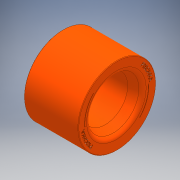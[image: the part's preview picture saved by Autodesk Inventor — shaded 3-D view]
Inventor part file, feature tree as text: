
AUTODESK INVENTOR PART (.ipt)
format: ipt  version: 2019.4 (Build 234330000, 330)  size: 897,536 bytes
history: native  units: mm
features: fillet x5, revolve x1, plane x1, emboss x1, sketch x1
ambient origin geometry x8: Origin, YZ Plane, XZ Plane, XY Plane, X Axis, Y Axis, Z Axis, Center Point
bodies: Solid1 (feature_tree)
feature tree (9):
  revolve  "Revolution1"  [1 undecoded]
  fillet  "Fillet8"  Radius=69.5mm
  fillet  "Fillet9"  Radius=63.0mm
  fillet  "Fillet10"  Radius=7.0mm
  fillet  "Fillet11"  Radius=7.0mm
  fillet  "Fillet12"  Radius=6.0mm
  plane  "Work Plane2"
  emboss  "Emboss1"
  sketch  "Sketch1"  dims[d2=90.0deg d27=46.5mm d29=69.5mm d31=63.0mm d32=7.0mm d33=7.0mm d34=6.0mm d35=55.0mm d39=80.0mm d40=1.4mm d42=5.6mm d44=19.0mm d45=19.0mm d46=56.0mm d47=0.872665mm d48=0.872665mm d49=12.5mm d50=5.0mm d54=0.5mm d55=0.1mm d56=0.0mm]
note: 1 required parameter value undecoded (feature->parameter linkage not recoverable at this tier; creation-order binding heuristic only, values carry confidence <= 0.55)
